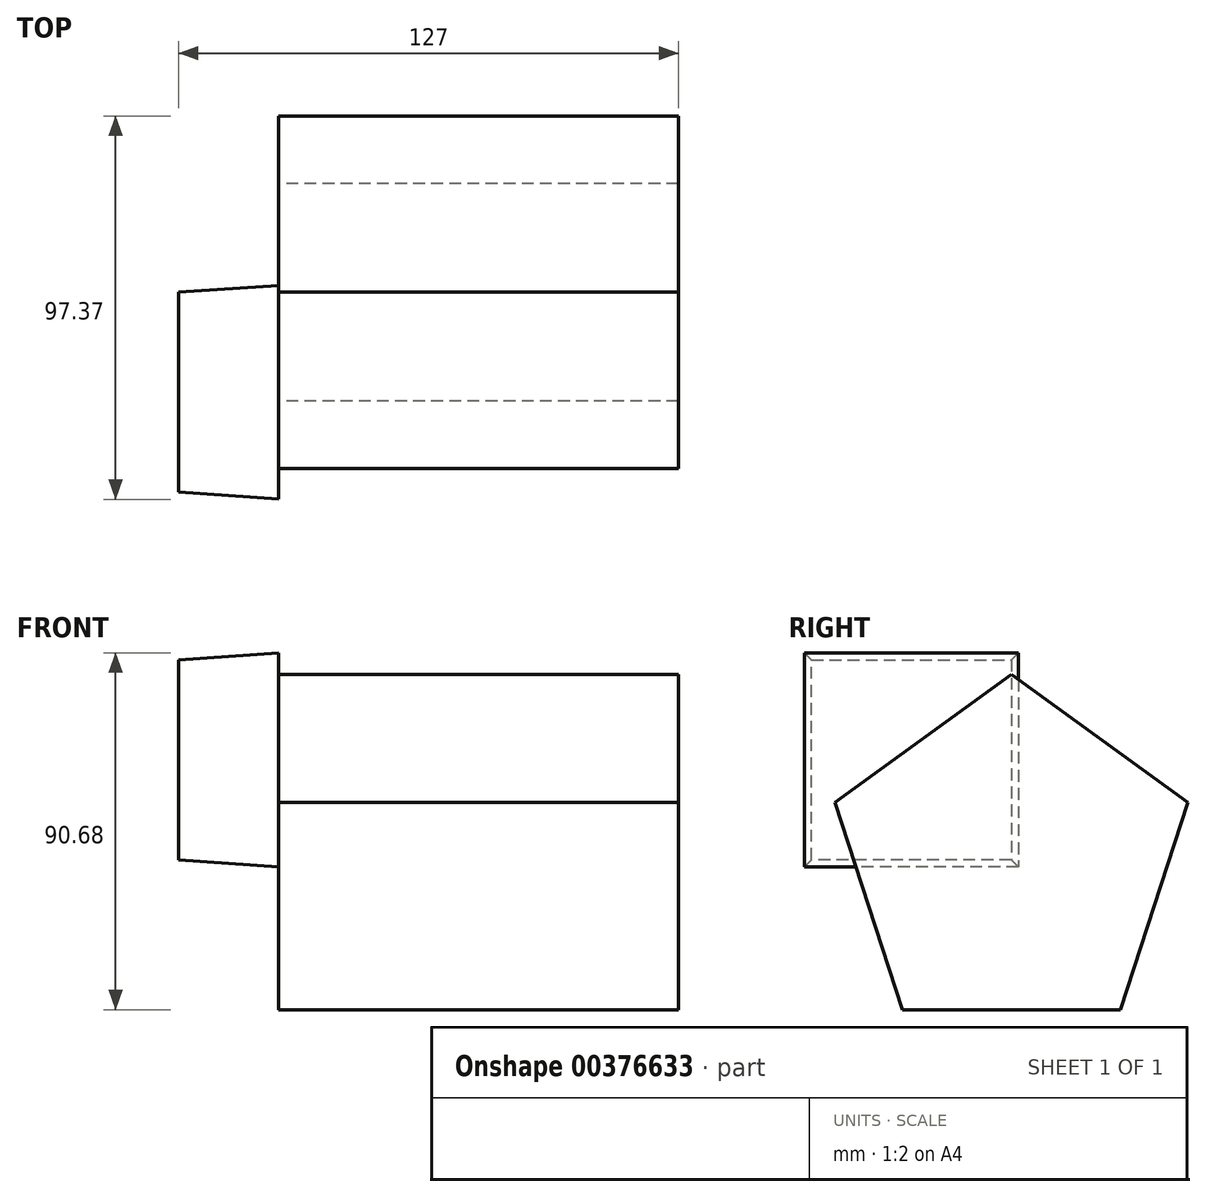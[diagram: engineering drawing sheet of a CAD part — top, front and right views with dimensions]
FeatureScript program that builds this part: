
annotation { "Feature Type Name" : "Feature", "Feature Type Description" : "" }
export const myFeature = defineFeature(function(context is Context, id is Id, definition is map)
    precondition{}
    {
        {
            var Q0;
            Q0=qCreatedBy(makeId("Right.planeOp"),FACE);
            var sketch = newSketch(context, id + "F0", { "sketchPlane" : qUnion([Q0])});
            skLineSegment(sketch, "E0.bottom", {"start": v(0, 0) * mm, "end": v(-50.8, 0) * mm});
            skLineSegment(sketch, "E0.top", {"start": v(0, 50.8) * mm, "end": v(-50.8, 50.8) * mm});
            skLineSegment(sketch, "E0.left", {"start": v(0, 0) * mm, "end": v(0, 50.8) * mm});
            skLineSegment(sketch, "E0.right", {"start": v(-50.8, 0) * mm, "end": v(-50.8, 50.8) * mm});
            skSolve(sketch);
        }
        {
            var Q0;
            Q0 = qSketchRegion(id + "F0", true);
            extrude(context, id + "F1", {"entities" : qUnion([Q0]), "depth" : 25.4 * mm, "hasDraft" : true, "draftAngle" : 4 * degree});
        }
        {
            var Q0;
            Q0=makeQuery(id+"F1.opExtrude","CAP_FACE",FACE,{"disambiguationData":[OSD([sQuery(id+"F0.wireOp",EDGE,"E0.bottom"),sQuery(id+"F0.wireOp",EDGE,"E0.top"),sQuery(id+"F0.wireOp",EDGE,"E0.left"),sQuery(id+"F0.wireOp",EDGE,"E0.right")])],"isStart":false});
            var sketch = newSketch(context, id + "F2", { "sketchPlane" : qUnion([Q0])});
            skPoint(sketch, "E1.0.midPoint", {"position": v(108.24, -43.9) * mm});
            skPoint(sketch, "E2.orphan", {"position": v(108.7, 48.8) * mm});
            skPoint(sketch, "E1.1.start.orphan", {"position": v(107.78, -136.59) * mm});
            skCircle(sketch, "E3.cCircle", {"center": v(0, 0) * mm, "radius": 38.1 * mm, "construction": true});
            skLineSegment(sketch, "E3.0", {"start": v(27.68, -38.1) * mm, "end": v(-27.68, -38.1) * mm});
            skLineSegment(sketch, "E3.1", {"start": v(-27.68, -38.1) * mm, "end": v(-44.79, 14.55) * mm});
            skLineSegment(sketch, "E3.2", {"start": v(-44.79, 14.55) * mm, "end": v(0, 47.1) * mm});
            skLineSegment(sketch, "E3.3", {"start": v(0, 47.1) * mm, "end": v(44.79, 14.55) * mm});
            skLineSegment(sketch, "E3.4", {"start": v(44.79, 14.55) * mm, "end": v(27.68, -38.1) * mm});
            skPoint(sketch, "E3.0.midPoint", {"position": v(0, -38.1) * mm});
            skSolve(sketch);
        }
        {
            var Q0;
            Q0 = qSketchRegion(id + "F2", true);
            extrude(context, id + "F3", {"entities" : qUnion([Q0]), "operationType" : NewBodyOperationType.ADD, "depth" : 101.6 * mm});
        }
    });
